# Revit family: 3-518-xxx - 37-518-xxx - Magnum (Wall Sconce)
name_source: partatom
category: Lighting Fixtures
revit_build: Autodesk Revit 2018 (Build: 20170223_1515(x64)
units: mm (PartAtom-declared; Revit-internal decimal feet)

## family parameters
Cut with Voids When Loaded = No
Host = Face
Light Source = Yes
Part Type = Normal
Room Calculation Point = No
Round Connector Dimension = Use Diameter
Shared = No

## types (8) — shared parameters
Color Filter = 16777215
Dimming Lamp Color Temperature Shift = <None>
Emit Shape Visible in Rendering = No
Emit from Rectangle Length = 30 "
Emit from Rectangle Width = 10 "
Lamp = LED Array
Manufacturer = Oxygen Lighting
Model = 3-518-xxx / 37-518-xxx - Magnum
Other = <By Category>
Photometric Web File = 3-518-24 Magnum Sconce.ies
Tilt Angle = 0.00°
URL = www.oxygenlighting.com
Wattage Comments = 15.1 W at 120 V
zero-valued in all types: Default Elevation

## per-type parameters (varying)
| type | Diffuser | Metal Finish |
| 3-518-14 / 37-518-14 - Magnum | Oxygen Lighting - Diffuser - Matte White Acrylic | Oxygen Lighting - Metal Finish - 14 - Polished Chrome |
| 3-518-24 / 37-518-24 - Magnum | Oxygen Lighting - Diffuser - Matte White Acrylic | Oxygen Lighting - Metal Finish - 24 - Satin Nickel |
| 3-518-25 / 37-518-25 - Magnum | Oxygen Lighting - Diffuser - Matte White Acrylic | Oxygen Lighting - Metal Finish - 25 - Satin Copper |
| 3-518-40 / 37-518-40 - Magnum | Oxygen Lighting - Diffuser - Matte White Acrylic | Oxygen Lighting - Metal Finish - 40 - Aged Brass |
| 3-518-114 / 37-518-114 - Magnum | Oxygen Lighting - Diffuser - White Opal Glass | Oxygen Lighting - Metal Finish - 14 - Polished Chrome |
| 3-518-124 / 37-518-124 - Magnum | Oxygen Lighting - Diffuser - White Opal Glass | Oxygen Lighting - Metal Finish - 24 - Satin Nickel |
| 3-518-125 / 37-518-125 - Magnum | Oxygen Lighting - Diffuser - White Opal Glass | Oxygen Lighting - Metal Finish - 25 - Satin Copper |
| 3-518-140 / 37-518-140 - Magnum | Oxygen Lighting - Diffuser - White Opal Glass | Oxygen Lighting - Metal Finish - 40 - Aged Brass |

## geometry (parser evidence)
native form markers: Sweep x7
no freeform markers — native parametric forms only
